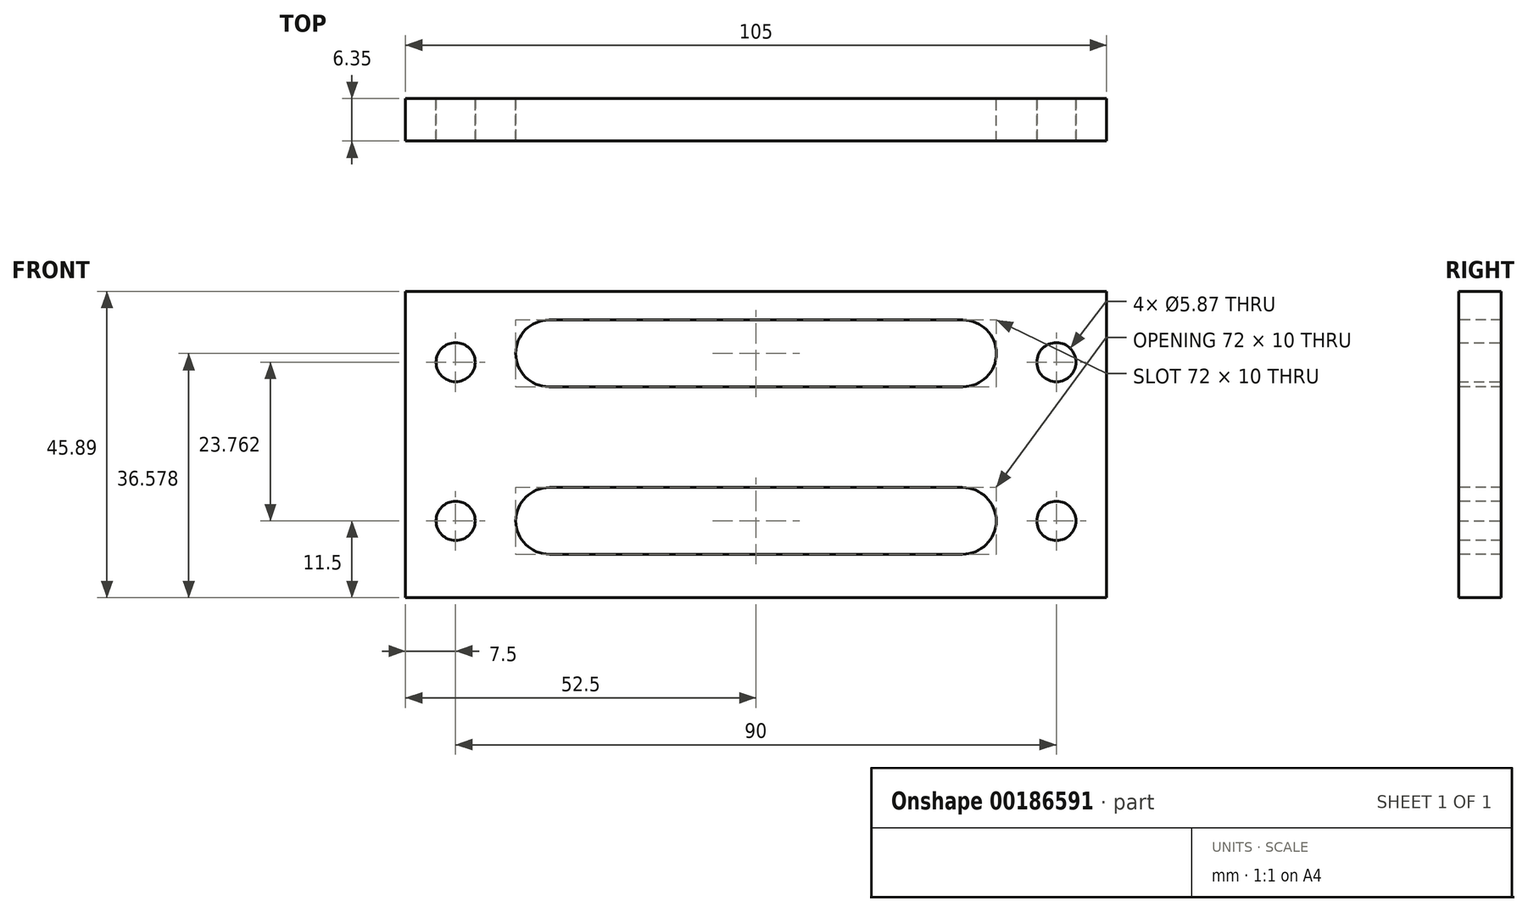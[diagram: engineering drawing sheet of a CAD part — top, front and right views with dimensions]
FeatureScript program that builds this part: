
annotation { "Feature Type Name" : "Feature", "Feature Type Description" : "" }
export const myFeature = defineFeature(function(context is Context, id is Id, definition is map)
    precondition{}
    {
        {
            var Q0;
            Q0=qCreatedBy(makeId("Front.planeOp"),FACE);
            var sketch = newSketch(context, id + "F0", { "sketchPlane" : qUnion([Q0])});
            skLineSegment(sketch, "E0.bottom", {"start": v(52.5, 11.5) * mm, "end": v(-52.5, 11.5) * mm});
            skLineSegment(sketch, "E0.top", {"start": v(52.5, -11.5) * mm, "end": v(-52.5, -11.5) * mm});
            skLineSegment(sketch, "E0.left", {"start": v(52.5, 11.5) * mm, "end": v(52.5, -11.5) * mm});
            skLineSegment(sketch, "E0.right", {"start": v(-52.5, 11.5) * mm, "end": v(-52.5, -11.5) * mm});
            skPoint(sketch, "E0.middle", {"position": v(0, 0) * mm});
            skSolve(sketch);
        }
        {
            var Q0;
            Q0=qSketchRegion(id+"F0",true);
            extrude(context, id + "F1", {"entities" : qUnion([Q0]), "depth" : 6.35 * mm});
        }
        {
            var Q0;
            Q0=makeQuery(id+"F1.opExtrude","CAP_FACE",FACE,{"disambiguationData":[OSD([sQuery(id+"F0.wireOp",EDGE,"E0.bottom"),sQuery(id+"F0.wireOp",EDGE,"E0.top"),sQuery(id+"F0.wireOp",EDGE,"E0.left"),sQuery(id+"F0.wireOp",EDGE,"E0.right")])],"isStart":false});
            var sketch = newSketch(context, id + "F2", { "sketchPlane" : qUnion([Q0])});
            skLineSegment(sketch, "E1.bottom", {"start": v(36, 5) * mm, "end": v(-36, 5) * mm});
            skLineSegment(sketch, "E1.top", {"start": v(36, -5) * mm, "end": v(-36, -5) * mm});
            skLineSegment(sketch, "E1.left", {"start": v(36, 5) * mm, "end": v(36, -5) * mm});
            skLineSegment(sketch, "E1.right", {"start": v(-36, 5) * mm, "end": v(-36, -5) * mm});
            skPoint(sketch, "E1.middle", {"position": v(0, 0) * mm});
            skSolve(sketch);
        }
        {
            var Q0;
            Q0=qSketchRegion(id+"F2",true);
            extrude(context, id + "F3", {"entities" : qUnion([Q0]), "operationType" : NewBodyOperationType.REMOVE, "oppositeDirection" : true, "depth" : 25.4 * mm});
        }
        {
            var Q0;
            Q0=makeQuery(id+"F1.opExtrude","CAP_FACE",FACE,{"disambiguationData":[OSD([sQuery(id+"F0.wireOp",EDGE,"E0.bottom"),sQuery(id+"F0.wireOp",EDGE,"E0.top"),sQuery(id+"F0.wireOp",EDGE,"E0.left"),sQuery(id+"F0.wireOp",EDGE,"E0.right")])],"isStart":false});
            var sketch = newSketch(context, id + "F4", { "sketchPlane" : qUnion([Q0])});
            skCircle(sketch, "E2", {"center": v(-45, 0) * mm, "radius": 2.93 * mm});
            skCircle(sketch, "E3.MirrorC", {"center": v(45, 0) * mm, "radius": 2.93 * mm});
            skSolve(sketch);
        }
        {
            var Q0;
            Q0=qSketchRegion(id+"F4",true);
            extrude(context, id + "F5", {"entities" : qUnion([Q0]), "operationType" : NewBodyOperationType.REMOVE, "oppositeDirection" : true, "depth" : 25.4 * mm});
        }
        {
            var Q0;
            Q0=makeQuery(id+"F3.boolean.opBoolean","COPY",EDGE,{"derivedFrom":makeQuery(id+"F3.opExtrude","SWEPT_EDGE",EDGE,{"disambiguationData":[OSD([sQuery(id+"F2.wireOp",EDGE,"E1.top"),sQuery(id+"F2.wireOp",EDGE,"E1.left")])]})});
            var Q1;
            Q1=makeQuery(id+"F3.boolean.opBoolean","COPY",EDGE,{"derivedFrom":makeQuery(id+"F3.opExtrude","SWEPT_EDGE",EDGE,{"disambiguationData":[OSD([sQuery(id+"F2.wireOp",EDGE,"E1.bottom"),sQuery(id+"F2.wireOp",EDGE,"E1.right")])]})});
            var Q2;
            Q2=makeQuery(id+"F3.boolean.opBoolean","COPY",EDGE,{"derivedFrom":makeQuery(id+"F3.opExtrude","SWEPT_EDGE",EDGE,{"disambiguationData":[OSD([sQuery(id+"F2.wireOp",EDGE,"E1.top"),sQuery(id+"F2.wireOp",EDGE,"E1.right")])]})});
            var Q3;
            Q3=makeQuery(id+"F3.boolean.opBoolean","COPY",EDGE,{"derivedFrom":makeQuery(id+"F3.opExtrude","SWEPT_EDGE",EDGE,{"disambiguationData":[OSD([sQuery(id+"F2.wireOp",EDGE,"E1.bottom"),sQuery(id+"F2.wireOp",EDGE,"E1.left")])]})});
            fillet(context, id + "F6", {"entities" : qUnion([Q0, Q1, Q2, Q3]), "radius" : 5.08 * mm, "tangentPropagation" : true, "allowEdgeOverflow" : false});
        }
        {
            var Q0;
            Q0=qCreatedBy(makeId("Front.planeOp"),FACE);
            var sketch = newSketch(context, id + "F7", { "sketchPlane" : qUnion([Q0])});
            skLineSegment(sketch, "E4.bottom", {"start": v(-52.5, 11.4) * mm, "end": v(52.5, 11.4) * mm});
            skLineSegment(sketch, "E4.top", {"start": v(-52.5, 34.4) * mm, "end": v(52.5, 34.4) * mm});
            skLineSegment(sketch, "E4.left", {"start": v(-52.5, 11.4) * mm, "end": v(-52.5, 34.4) * mm});
            skLineSegment(sketch, "E4.right", {"start": v(52.5, 11.4) * mm, "end": v(52.5, 34.4) * mm});
            skCircle(sketch, "E5", {"center": v(-45, 23.76) * mm, "radius": 2.93 * mm});
            skCircle(sketch, "E6", {"center": v(45, 23.76) * mm, "radius": 2.93 * mm});
            skSolve(sketch);
        }
        {
            var Q0;
            Q0 = qSketchRegion(id + "F7", true);
            extrude(context, id + "F8", {"entities" : qUnion([Q0]), "operationType" : NewBodyOperationType.ADD, "depth" : 6.35 * mm});
        }
        {
            var Q0;
            Q0=makeQuery(id+"F8.boolean.opBoolean","MERGE",FACE,{"derivedFrom":[makeQuery(id+"F1.opExtrude","CAP_FACE",FACE,{"disambiguationData":[OSD([sQuery(id+"F0.wireOp",EDGE,"E0.bottom"),sQuery(id+"F0.wireOp",EDGE,"E0.top"),sQuery(id+"F0.wireOp",EDGE,"E0.left"),sQuery(id+"F0.wireOp",EDGE,"E0.right")])],"isStart":false}),makeQuery(id+"F8.opExtrude","CAP_FACE",FACE,{"disambiguationData":[OSD([sQuery(id+"F7.wireOp",EDGE,"E4.bottom"),sQuery(id+"F7.wireOp",EDGE,"E4.top"),sQuery(id+"F7.wireOp",EDGE,"E4.left"),sQuery(id+"F7.wireOp",EDGE,"E4.right"),sQuery(id+"F7.wireOp",EDGE,"E5"),sQuery(id+"F7.wireOp",EDGE,"E6")])],"isStart":false})]});
            var sketch = newSketch(context, id + "F9", { "sketchPlane" : qUnion([Q0])});
            skLineSegment(sketch, "E7.bottom", {"start": v(36, 30.08) * mm, "end": v(-36, 30.08) * mm});
            skLineSegment(sketch, "E7.top", {"start": v(36, 20.08) * mm, "end": v(-36, 20.08) * mm});
            skLineSegment(sketch, "E7.left", {"start": v(36, 30.08) * mm, "end": v(36, 20.08) * mm});
            skLineSegment(sketch, "E7.right", {"start": v(-36, 30.08) * mm, "end": v(-36, 20.08) * mm});
            skPoint(sketch, "E7.middle", {"position": v(0, 25.08) * mm});
            skSolve(sketch);
        }
        {
            var Q0;
            Q0 = qSketchRegion(id + "F9", true);
            extrude(context, id + "F10", {"entities" : qUnion([Q0]), "operationType" : NewBodyOperationType.REMOVE, "oppositeDirection" : true, "depth" : 25 * mm});
        }
        {
            var Q0;
            Q0=makeQuery(id+"F10.boolean.opBoolean","COPY",EDGE,{"derivedFrom":makeQuery(id+"F10.opExtrude","SWEPT_EDGE",EDGE,{"disambiguationData":[OSD([sQuery(id+"F9.wireOp",EDGE,"E7.top"),sQuery(id+"F9.wireOp",EDGE,"E7.right")])]})});
            var Q1;
            Q1=makeQuery(id+"F10.boolean.opBoolean","COPY",EDGE,{"derivedFrom":makeQuery(id+"F10.opExtrude","SWEPT_EDGE",EDGE,{"disambiguationData":[OSD([sQuery(id+"F9.wireOp",EDGE,"E7.top"),sQuery(id+"F9.wireOp",EDGE,"E7.left")])]})});
            var Q2;
            Q2=makeQuery(id+"F10.boolean.opBoolean","COPY",EDGE,{"derivedFrom":makeQuery(id+"F10.opExtrude","SWEPT_EDGE",EDGE,{"disambiguationData":[OSD([sQuery(id+"F9.wireOp",EDGE,"E7.bottom"),sQuery(id+"F9.wireOp",EDGE,"E7.left")])]})});
            var Q3;
            Q3=makeQuery(id+"F10.boolean.opBoolean","COPY",EDGE,{"derivedFrom":makeQuery(id+"F10.opExtrude","SWEPT_EDGE",EDGE,{"disambiguationData":[OSD([sQuery(id+"F9.wireOp",EDGE,"E7.bottom"),sQuery(id+"F9.wireOp",EDGE,"E7.right")])]})});
            fillet(context, id + "F11", {"entities" : qUnion([Q0, Q1, Q2, Q3]), "radius" : 5 * mm, "tangentPropagation" : true, "allowEdgeOverflow" : false});
        }
    });
